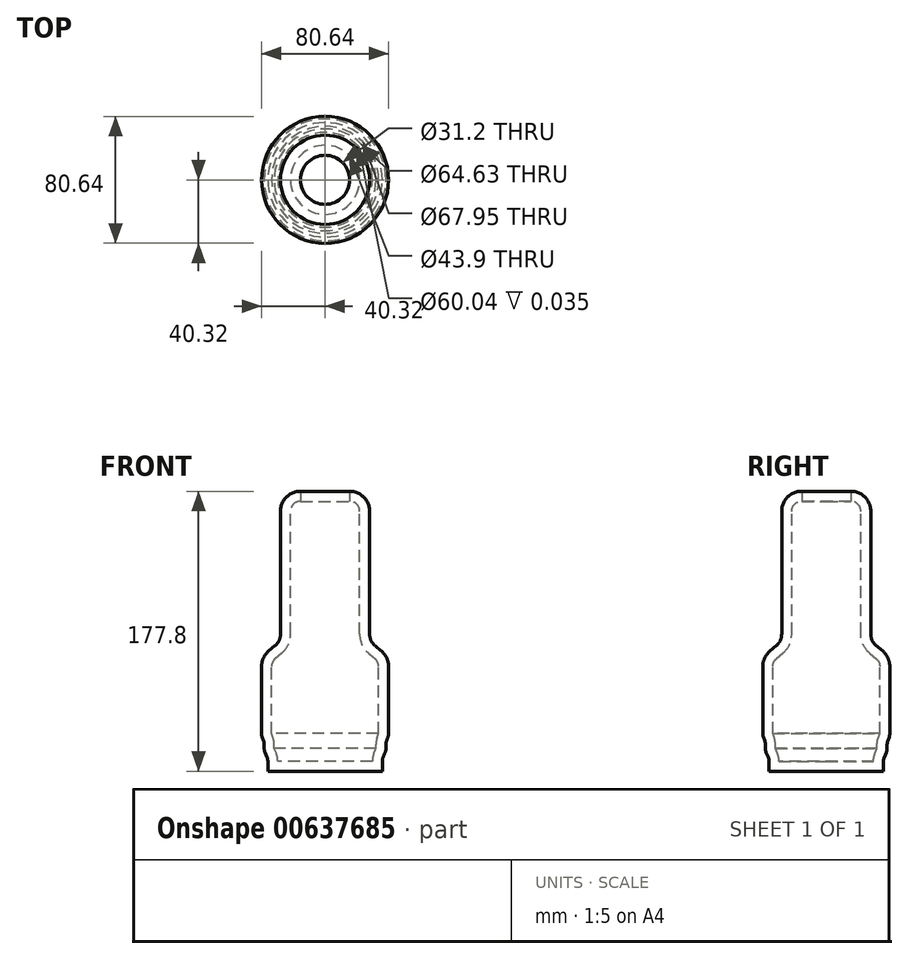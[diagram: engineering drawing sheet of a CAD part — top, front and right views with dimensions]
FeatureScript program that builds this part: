
annotation { "Feature Type Name" : "Feature", "Feature Type Description" : "" }
export const myFeature = defineFeature(function(context is Context, id is Id, definition is map)
    precondition{}
    {
        {
            var Q0;
            Q0=qCreatedBy(makeId("Front.planeOp"),FACE);
            var sketch = newSketch(context, id + "F0", { "sketchPlane" : qUnion([Q0])});
            skLineSegment(sketch, "E0", {"start": v(0, 0) * mm, "end": v(36.37, 0) * mm});
            skLineSegment(sketch, "E1", {"start": v(36.37, 0) * mm, "end": v(36.37, 6.39) * mm});
            skLineSegment(sketch, "E2", {"start": v(36.85, 8.8) * mm, "end": v(38.19, 12.05) * mm});
            skLineSegment(sketch, "E3", {"start": v(38.67, 14.47) * mm, "end": v(38.67, 17) * mm});
            skLineSegment(sketch, "E4", {"start": v(39.03, 19.12) * mm, "end": v(39.96, 21.72) * mm});
            skLineSegment(sketch, "E5", {"start": v(40.32, 23.85) * mm, "end": v(40.32, 66.54) * mm});
            skLineSegment(sketch, "E6", {"start": v(35.83, 76.24) * mm, "end": v(31.67, 79.76) * mm});
            skLineSegment(sketch, "E7", {"start": v(28.3, 87.03) * mm, "end": v(28.3, 177.8) * mm});
            skLineSegment(sketch, "E8", {"start": v(28.3, 177.8) * mm, "end": v(0, 177.8) * mm});
            skLineSegment(sketch, "E9", {"start": v(0, 177.8) * mm, "end": v(0, 0) * mm});
            skPoint(sketch, "E10.visualSharp", {"position": v(36.37, 7.64) * mm});
            skArc(sketch, "E10.filletArc", {"start": v(36.85, 8.8) * mm, "mid": v(36.49, 7.62) * mm, "end": v(36.37, 6.39) * mm});
            skPoint(sketch, "E11.visualSharp", {"position": v(38.67, 13.21) * mm});
            skArc(sketch, "E11.filletArc", {"start": v(38.19, 12.05) * mm, "mid": v(38.54, 13.24) * mm, "end": v(38.67, 14.47) * mm});
            skPoint(sketch, "E12.visualSharp", {"position": v(38.67, 18.09) * mm});
            skArc(sketch, "E12.filletArc", {"start": v(39.03, 19.12) * mm, "mid": v(38.76, 18.07) * mm, "end": v(38.67, 17) * mm});
            skPoint(sketch, "E13.visualSharp", {"position": v(40.32, 22.75) * mm});
            skArc(sketch, "E13.filletArc", {"start": v(39.96, 21.72) * mm, "mid": v(40.23, 22.77) * mm, "end": v(40.32, 23.85) * mm});
            skPoint(sketch, "E14.visualSharp", {"position": v(40.32, 72.43) * mm});
            skArc(sketch, "E14.filletArc", {"start": v(40.32, 66.54) * mm, "mid": v(39.15, 71.88) * mm, "end": v(35.83, 76.24) * mm});
            skPoint(sketch, "E15.visualSharp", {"position": v(28.3, 82.61) * mm});
            skArc(sketch, "E15.filletArc", {"start": v(28.3, 87.03) * mm, "mid": v(29.18, 83.02) * mm, "end": v(31.67, 79.76) * mm});
            skSolve(sketch);
        }
        {
            var Q0;
            Q0 = qSketchRegion(id + "F0", true);
            var Q1;
            Q1=sQuery(id+"F0.wireOp",EDGE,"E9");
            revolve(context, id + "F1", {"entities" : qUnion([Q0]), "axis" : qUnion([Q1]), "revolveType" : RevolveType.FULL});
        }
        {
            var Q0;
            Q0=makeQuery(id+"F1.opRevolve","SWEPT_EDGE",EDGE,{"disambiguationData":[OSD([sQuery(id+"F0.wireOp",EDGE,"E7"),sQuery(id+"F0.wireOp",EDGE,"E8")])]});
            fillet(context, id + "F2", {"entities" : qUnion([Q0]), "radius" : 12.7 * mm, "tangentPropagation" : true, "allowEdgeOverflow" : false});
        }
        {
            var Q0;
            Q0=makeQuery(id+"F1.opRevolve","SWEPT_FACE",FACE,{"disambiguationData":[OSD([sQuery(id+"F0.wireOp",EDGE,"E8")])]});
            shell(context, id + "F3", {"entities" : qUnion([Q0]), "thickness" : 6.35 * mm});
        }
    });
